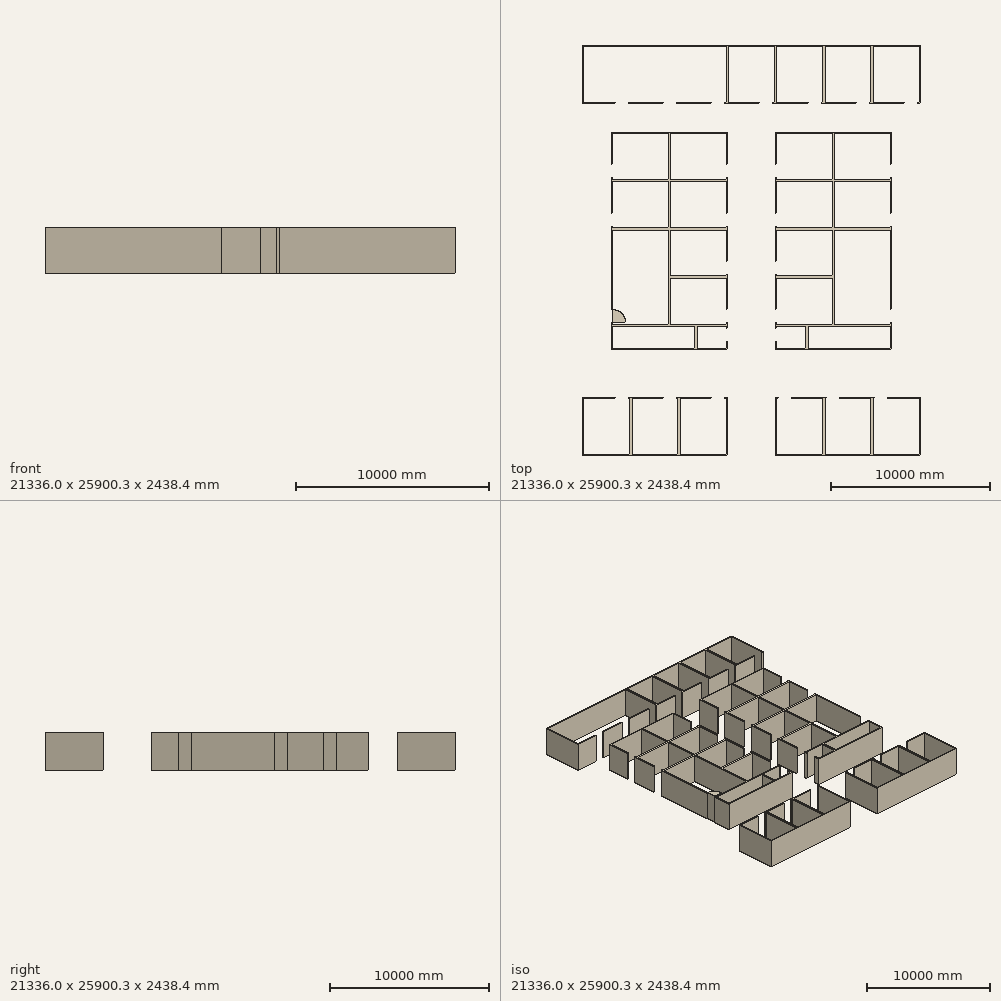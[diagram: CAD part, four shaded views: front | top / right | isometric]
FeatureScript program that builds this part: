
annotation { "Feature Type Name" : "Feature", "Feature Type Description" : "" }
export const myFeature = defineFeature(function(context is Context, id is Id, definition is map)
    precondition{}
    {
        {
            var Q0;
            Q0=qCreatedBy(makeId("Top.planeOp"),FACE);
            var sketch = newSketch(context, id + "F0", { "sketchPlane" : qUnion([Q0])});
            skLineSegment(sketch, "E0.bottom", {"start": v(7665, -2192.75) * mm, "end": v(10713, -2192.75) * mm});
            skLineSegment(sketch, "E0.top", {"start": v(7665, 1464.85) * mm, "end": v(10713, 1464.85) * mm});
            skLineSegment(sketch, "E0.left", {"start": v(7665, -2192.75) * mm, "end": v(7665, 1464.85) * mm});
            skLineSegment(sketch, "E0.right", {"start": v(10713, -2192.75) * mm, "end": v(10713, 1464.85) * mm});
            skLineSegment(sketch, "E1.left", {"start": v(10713, 1464.85) * mm, "end": v(10713, -2192.75) * mm});
            skLineSegment(sketch, "E2.bottom", {"start": v(7665, 6029.3) * mm, "end": v(11322.6, 6029.3) * mm});
            skLineSegment(sketch, "E2.top", {"start": v(7665, 9077.3) * mm, "end": v(11322.6, 9077.3) * mm});
            skLineSegment(sketch, "E2.left", {"start": v(7665, 6029.3) * mm, "end": v(7665, 9077.3) * mm});
            skLineSegment(sketch, "E2.right", {"start": v(11322.6, 6029.3) * mm, "end": v(11322.6, 9077.3) * mm});
            skLineSegment(sketch, "E3.bottom", {"start": v(11322.6, 6029.3) * mm, "end": v(14980.2, 6029.3) * mm});
            skLineSegment(sketch, "E4.bottom", {"start": v(7665, 6029.3) * mm, "end": v(9643.15, 6029.3) * mm});
            skLineSegment(sketch, "E4.top", {"start": v(7665, 4505.3) * mm, "end": v(9643.15, 4505.3) * mm});
            skLineSegment(sketch, "E4.left", {"start": v(7665, 6029.3) * mm, "end": v(7665, 4505.3) * mm});
            skLineSegment(sketch, "E4.right", {"start": v(9643.15, 6029.3) * mm, "end": v(9643.15, 4505.3) * mm});
            skLineSegment(sketch, "E5.bottom", {"start": v(9643.15, 4505.3) * mm, "end": v(14980.2, 4505.3) * mm});
            skLineSegment(sketch, "E5.top", {"start": v(9643.15, 6029.3) * mm, "end": v(14980.2, 6029.3) * mm});
            skLineSegment(sketch, "E5.left", {"start": v(9643.15, 4505.3) * mm, "end": v(9643.15, 6029.3) * mm});
            skLineSegment(sketch, "E5.right", {"start": v(14980.2, 4505.3) * mm, "end": v(14980.2, 6029.3) * mm});
            skLineSegment(sketch, "E6.0", {"start": v(7741.2, -2116.55) * mm, "end": v(10636.8, -2116.55) * mm});
            skLineSegment(sketch, "E6.1", {"start": v(7741.2, -2116.55) * mm, "end": v(7741.2, 1388.65) * mm});
            skLineSegment(sketch, "E6.2", {"start": v(7741.2, 1388.65) * mm, "end": v(10636.8, 1388.65) * mm});
            skLineSegment(sketch, "E6.3", {"start": v(10636.8, 1388.65) * mm, "end": v(10636.8, -2116.55) * mm});
            skLineSegment(sketch, "E7", {"start": v(7842.8, 1388.65) * mm, "end": v(7842.8, 1464.85) * mm});
            skLineSegment(sketch, "E8", {"start": v(8655.6, 1388.65) * mm, "end": v(8655.6, 1464.85) * mm});
            skLineSegment(sketch, "E9", {"start": v(8655.6, 1388.65) * mm, "end": v(8655.6, 575.85) * mm});
            skArc(sketch, "E10", {"start": v(8655.6, 575.85) * mm, "mid": v(8080.86, 813.91) * mm, "end": v(7842.8, 1388.65) * mm});
            skLineSegment(sketch, "E11.0", {"start": v(7741.2, 9001.1) * mm, "end": v(11246.4, 9001.1) * mm});
            skLineSegment(sketch, "E11.1", {"start": v(7741.2, 6105.5) * mm, "end": v(7741.2, 9001.1) * mm});
            skLineSegment(sketch, "E11.2", {"start": v(7741.2, 6105.5) * mm, "end": v(11246.4, 6105.5) * mm});
            skLineSegment(sketch, "E11.3", {"start": v(11246.4, 6105.5) * mm, "end": v(11246.4, 9001.1) * mm});
            skLineSegment(sketch, "E12", {"start": v(7741.2, 6207.1) * mm, "end": v(7665, 6207.1) * mm});
            skLineSegment(sketch, "E13", {"start": v(7741.2, 7019.9) * mm, "end": v(7665, 7019.9) * mm});
            skLineSegment(sketch, "E14", {"start": v(7741.2, 7019.9) * mm, "end": v(8554, 7019.9) * mm});
            skArc(sketch, "E15", {"start": v(8554, 7019.9) * mm, "mid": v(8315.93, 6445.17) * mm, "end": v(7741.2, 6207.1) * mm});
            skArc(sketch, "E16.0.1.0", {"start": v(8554, 10067.9) * mm, "mid": v(8315.93, 9493.17) * mm, "end": v(7741.2, 9255.1) * mm});
            skLineSegment(sketch, "E16.0.1.1", {"start": v(7741.2, 12049.1) * mm, "end": v(11246.4, 12049.1) * mm});
            skLineSegment(sketch, "E16.0.1.2", {"start": v(11322.6, 9077.3) * mm, "end": v(11322.6, 12125.3) * mm});
            skLineSegment(sketch, "E16.0.1.3", {"start": v(7741.2, 10067.9) * mm, "end": v(8554, 10067.9) * mm});
            skLineSegment(sketch, "E16.0.1.6", {"start": v(11246.4, 9153.5) * mm, "end": v(11246.4, 12049.1) * mm});
            skLineSegment(sketch, "E16.0.1.10", {"start": v(7741.2, 9153.5) * mm, "end": v(11246.4, 9153.5) * mm});
            skLineSegment(sketch, "E16.0.1.13", {"start": v(11322.6, 9077.3) * mm, "end": v(11322.6, 12125.3) * mm});
            skLineSegment(sketch, "E16.0.1.14", {"start": v(7741.2, 9255.1) * mm, "end": v(7665, 9255.1) * mm});
            skLineSegment(sketch, "E16.0.1.15", {"start": v(7741.2, 10067.9) * mm, "end": v(7665, 10067.9) * mm});
            skArc(sketch, "E16.0.2.0", {"start": v(8554, 13115.9) * mm, "mid": v(8315.93, 12541.17) * mm, "end": v(7741.2, 12303.1) * mm});
            skLineSegment(sketch, "E16.0.2.1", {"start": v(7741.2, 15097.1) * mm, "end": v(11246.4, 15097.1) * mm});
            skLineSegment(sketch, "E16.0.2.2", {"start": v(11322.6, 12125.3) * mm, "end": v(11322.6, 14975.18) * mm});
            skLineSegment(sketch, "E16.0.2.3", {"start": v(7741.2, 13115.9) * mm, "end": v(8554, 13115.9) * mm});
            skLineSegment(sketch, "E16.0.2.6", {"start": v(11246.4, 12201.5) * mm, "end": v(11246.4, 15097.1) * mm});
            skLineSegment(sketch, "E16.0.2.7", {"start": v(7665, 12125.3) * mm, "end": v(7665, 14975.18) * mm});
            skLineSegment(sketch, "E16.0.2.10", {"start": v(7741.2, 12201.5) * mm, "end": v(11246.4, 12201.5) * mm});
            skLineSegment(sketch, "E16.0.2.11", {"start": v(7741.2, 12201.5) * mm, "end": v(7741.2, 15097.1) * mm});
            skLineSegment(sketch, "E16.0.2.13", {"start": v(11322.6, 12125.3) * mm, "end": v(11322.6, 15173.3) * mm});
            skLineSegment(sketch, "E16.0.2.14", {"start": v(7741.2, 12303.1) * mm, "end": v(7665, 12303.1) * mm});
            skLineSegment(sketch, "E16.0.2.15", {"start": v(7741.2, 13115.9) * mm, "end": v(7665, 13115.9) * mm});
            skArc(sketch, "E16.0.3.0", {"start": v(8554, 16163.9) * mm, "mid": v(8315.93, 15589.17) * mm, "end": v(7741.2, 15351.1) * mm});
            skLineSegment(sketch, "E16.0.3.1", {"start": v(7741.2, 18145.1) * mm, "end": v(11246.4, 18145.1) * mm});
            skLineSegment(sketch, "E16.0.3.2", {"start": v(11322.6, 15173.3) * mm, "end": v(11322.6, 18221.3) * mm});
            skLineSegment(sketch, "E16.0.3.3", {"start": v(7741.2, 16163.9) * mm, "end": v(8554, 16163.9) * mm});
            skLineSegment(sketch, "E16.0.3.4", {"start": v(7665, 15173.3) * mm, "end": v(11322.6, 15173.3) * mm});
            skLineSegment(sketch, "E16.0.3.6", {"start": v(11246.4, 15249.5) * mm, "end": v(11246.4, 18145.1) * mm});
            skLineSegment(sketch, "E16.0.3.7", {"start": v(7665, 15173.3) * mm, "end": v(7665, 18221.3) * mm});
            skLineSegment(sketch, "E16.0.3.8", {"start": v(7665, 18221.3) * mm, "end": v(11322.6, 18221.3) * mm});
            skLineSegment(sketch, "E16.0.3.10", {"start": v(7741.2, 15249.5) * mm, "end": v(11246.4, 15249.5) * mm});
            skLineSegment(sketch, "E16.0.3.11", {"start": v(7741.2, 15249.5) * mm, "end": v(7741.2, 18145.1) * mm});
            skLineSegment(sketch, "E16.0.3.12", {"start": v(7665, 18221.3) * mm, "end": v(11322.6, 18221.3) * mm});
            skLineSegment(sketch, "E16.0.3.13", {"start": v(11322.6, 15173.3) * mm, "end": v(11322.6, 18221.3) * mm});
            skLineSegment(sketch, "E16.0.3.14", {"start": v(7741.2, 15351.1) * mm, "end": v(7665, 15351.1) * mm});
            skLineSegment(sketch, "E16.0.3.15", {"start": v(7741.2, 16163.9) * mm, "end": v(7665, 16163.9) * mm});
            skLineSegment(sketch, "E16.direction1", {"start": v(7665, 6029.3) * mm, "end": v(7665, 6029.3) * mm});
            skLineSegment(sketch, "E16.direction2", {"start": v(7665, 6029.3) * mm, "end": v(7665, 9077.3) * mm, "construction": true});
            skLineSegment(sketch, "E17.left", {"start": v(11322.6, 6029.3) * mm, "end": v(11322.6, 12125.3) * mm});
            skLineSegment(sketch, "E18.MirrorCS", {"start": v(14904, 15351.1) * mm, "end": v(14980.2, 15351.1) * mm});
            skLineSegment(sketch, "E19.MirrorCS", {"start": v(14904, 12303.1) * mm, "end": v(14980.2, 12303.1) * mm});
            skLineSegment(sketch, "E20.MirrorCS", {"start": v(14904, 13115.9) * mm, "end": v(14980.2, 13115.9) * mm});
            skLineSegment(sketch, "E21.MirrorCS", {"start": v(14904, 16163.9) * mm, "end": v(14980.2, 16163.9) * mm});
            skLineSegment(sketch, "E22.MirrorCS", {"start": v(14980.2, 15173.3) * mm, "end": v(11322.6, 15173.3) * mm});
            skLineSegment(sketch, "E23.MirrorCS", {"start": v(14980.2, 18221.3) * mm, "end": v(11322.6, 18221.3) * mm});
            skLineSegment(sketch, "E24.MirrorCS", {"start": v(14904, 15097.1) * mm, "end": v(11398.8, 15097.1) * mm});
            skLineSegment(sketch, "E25.MirrorCS", {"start": v(14904, 18145.1) * mm, "end": v(11398.8, 18145.1) * mm});
            skArc(sketch, "E26.MirrorCS", {"start": v(14091.2, 13115.9) * mm, "mid": v(14329.26, 12541.17) * mm, "end": v(14904, 12303.1) * mm});
            skArc(sketch, "E27.MirrorCS", {"start": v(14091.2, 16163.9) * mm, "mid": v(14329.26, 15589.17) * mm, "end": v(14904, 15351.1) * mm});
            skLineSegment(sketch, "E28.MirrorCS", {"start": v(14980.2, 15173.3) * mm, "end": v(14980.2, 18221.3) * mm});
            skLineSegment(sketch, "E29.MirrorCS", {"start": v(14904, 13115.9) * mm, "end": v(14091.2, 13115.9) * mm});
            skLineSegment(sketch, "E30.MirrorCS", {"start": v(14904, 16163.9) * mm, "end": v(14091.2, 16163.9) * mm});
            skLineSegment(sketch, "E31.MirrorCS", {"start": v(14980.2, 12125.3) * mm, "end": v(14980.2, 14975.18) * mm});
            skLineSegment(sketch, "E32.MirrorCS", {"start": v(14980.2, 6029.3) * mm, "end": v(13002.04, 6029.3) * mm});
            skLineSegment(sketch, "E33.MirrorCS", {"start": v(11398.8, 12201.5) * mm, "end": v(11398.8, 15097.1) * mm});
            skLineSegment(sketch, "E34.MirrorCS", {"start": v(11398.8, 15249.5) * mm, "end": v(11398.8, 18145.1) * mm});
            skLineSegment(sketch, "E35.MirrorCS", {"start": v(14980.2, 6029.3) * mm, "end": v(11322.6, 6029.3) * mm});
            skLineSegment(sketch, "E36.MirrorCS", {"start": v(14904, 15249.5) * mm, "end": v(14904, 18145.1) * mm});
            skLineSegment(sketch, "E37.MirrorCS", {"start": v(14904, 12201.5) * mm, "end": v(14904, 15097.1) * mm});
            skLineSegment(sketch, "E38.MirrorCS", {"start": v(14904, 15249.5) * mm, "end": v(11398.8, 15249.5) * mm});
            skLineSegment(sketch, "E39.MirrorCS", {"start": v(14904, 12201.5) * mm, "end": v(11398.8, 12201.5) * mm});
            skLineSegment(sketch, "E40.MirrorCS", {"start": v(14980.2, 4505.3) * mm, "end": v(13002.04, 4505.3) * mm});
            skLineSegment(sketch, "E41.0", {"start": v(7741.2, 4581.5) * mm, "end": v(9566.95, 4581.5) * mm});
            skLineSegment(sketch, "E41.1", {"start": v(7741.2, 5953.1) * mm, "end": v(7741.2, 4581.5) * mm});
            skLineSegment(sketch, "E41.2", {"start": v(7741.2, 5953.1) * mm, "end": v(9566.95, 5953.1) * mm});
            skLineSegment(sketch, "E41.3", {"start": v(9566.95, 5953.1) * mm, "end": v(9566.95, 4581.5) * mm});
            skLineSegment(sketch, "E42.0", {"start": v(9719.35, 4581.5) * mm, "end": v(14904, 4581.5) * mm});
            skLineSegment(sketch, "E42.1", {"start": v(9719.35, 5953.1) * mm, "end": v(9719.35, 4581.5) * mm});
            skLineSegment(sketch, "E42.2", {"start": v(9719.35, 5953.1) * mm, "end": v(14904, 5953.1) * mm});
            skLineSegment(sketch, "E42.3", {"start": v(14904, 4581.5) * mm, "end": v(14904, 5953.1) * mm});
            skLineSegment(sketch, "E43", {"start": v(7741.2, 5851.5) * mm, "end": v(7665, 5851.5) * mm});
            skLineSegment(sketch, "E44", {"start": v(7741.2, 5038.7) * mm, "end": v(7665, 5038.7) * mm});
            skLineSegment(sketch, "E45", {"start": v(7741.2, 5851.5) * mm, "end": v(8554, 5851.5) * mm});
            skArc(sketch, "E46", {"start": v(8554, 5851.5) * mm, "mid": v(8315.93, 5276.77) * mm, "end": v(7741.2, 5038.7) * mm});
            skLineSegment(sketch, "E47.1.0.0", {"start": v(10789.2, -2116.55) * mm, "end": v(10789.2, 1388.65) * mm});
            skLineSegment(sketch, "E47.1.0.1", {"start": v(10789.2, 1388.65) * mm, "end": v(13684.8, 1388.65) * mm});
            skLineSegment(sketch, "E47.1.0.2", {"start": v(10789.2, -2116.55) * mm, "end": v(13684.8, -2116.55) * mm});
            skLineSegment(sketch, "E47.1.0.3", {"start": v(13684.8, 1388.65) * mm, "end": v(13684.8, -2116.55) * mm});
            skLineSegment(sketch, "E47.1.0.4", {"start": v(11703.6, 1388.65) * mm, "end": v(11703.6, 575.85) * mm});
            skLineSegment(sketch, "E47.1.0.5", {"start": v(10713, -2192.75) * mm, "end": v(13761, -2192.75) * mm});
            skLineSegment(sketch, "E47.1.0.6", {"start": v(10713, 1464.85) * mm, "end": v(13761, 1464.85) * mm});
            skArc(sketch, "E47.1.0.8", {"start": v(11703.6, 575.85) * mm, "mid": v(11128.86, 813.91) * mm, "end": v(10890.8, 1388.65) * mm});
            skLineSegment(sketch, "E47.1.0.9", {"start": v(13761, 1464.85) * mm, "end": v(13761, -2192.75) * mm});
            skLineSegment(sketch, "E47.1.0.10", {"start": v(10890.8, 1388.65) * mm, "end": v(10890.8, 1464.85) * mm});
            skLineSegment(sketch, "E47.1.0.11", {"start": v(11703.6, 1388.65) * mm, "end": v(11703.6, 1464.85) * mm});
            skLineSegment(sketch, "E47.1.0.12", {"start": v(13761, -2192.75) * mm, "end": v(13761, 1464.85) * mm});
            skLineSegment(sketch, "E47.2.0.0", {"start": v(13837.2, -2116.55) * mm, "end": v(13837.2, 1388.65) * mm});
            skLineSegment(sketch, "E47.2.0.1", {"start": v(13837.2, 1388.65) * mm, "end": v(16732.8, 1388.65) * mm});
            skLineSegment(sketch, "E47.2.0.2", {"start": v(13837.2, -2116.55) * mm, "end": v(16732.8, -2116.55) * mm});
            skLineSegment(sketch, "E47.2.0.3", {"start": v(16732.8, 1388.65) * mm, "end": v(16732.8, -2116.55) * mm});
            skLineSegment(sketch, "E47.2.0.4", {"start": v(14751.6, 1388.65) * mm, "end": v(14751.6, 575.85) * mm});
            skLineSegment(sketch, "E47.2.0.5", {"start": v(13761, -2192.75) * mm, "end": v(16809, -2192.75) * mm});
            skLineSegment(sketch, "E47.2.0.6", {"start": v(13761, 1464.85) * mm, "end": v(16809, 1464.85) * mm});
            skLineSegment(sketch, "E47.2.0.7", {"start": v(13761, -2192.75) * mm, "end": v(13761, 1464.85) * mm});
            skArc(sketch, "E47.2.0.8", {"start": v(14751.6, 575.85) * mm, "mid": v(14176.86, 813.91) * mm, "end": v(13938.8, 1388.65) * mm});
            skLineSegment(sketch, "E47.2.0.9", {"start": v(16809, 1464.85) * mm, "end": v(16809, -2192.75) * mm});
            skLineSegment(sketch, "E47.2.0.10", {"start": v(13938.8, 1388.65) * mm, "end": v(13938.8, 1464.85) * mm});
            skLineSegment(sketch, "E47.2.0.11", {"start": v(14751.6, 1388.65) * mm, "end": v(14751.6, 1464.85) * mm});
            skLineSegment(sketch, "E47.2.0.12", {"start": v(16809, -2192.75) * mm, "end": v(16809, 1464.85) * mm});
            skLineSegment(sketch, "E47.direction1", {"start": v(7665, -2192.75) * mm, "end": v(10713, -2192.75) * mm, "construction": true});
            skLineSegment(sketch, "E48.1.0.9", {"start": v(7665.05, 20128.44) * mm, "end": v(7665.05, 23786.04) * mm});
            skLineSegment(sketch, "E48.1.0.12", {"start": v(7665.05, 23707.55) * mm, "end": v(7665.05, 20049.95) * mm});
            skLineSegment(sketch, "E48.2.0.0", {"start": v(7588.85, 23631.35) * mm, "end": v(7588.85, 20126.15) * mm});
            skLineSegment(sketch, "E48.2.0.1", {"start": v(7588.85, 20126.15) * mm, "end": v(4693.25, 20126.15) * mm});
            skLineSegment(sketch, "E48.2.0.2", {"start": v(7588.85, 23631.35) * mm, "end": v(4693.25, 23631.35) * mm});
            skLineSegment(sketch, "E48.2.0.3", {"start": v(4693.25, 20126.15) * mm, "end": v(4693.25, 23631.35) * mm});
            skLineSegment(sketch, "E48.2.0.4", {"start": v(6674.45, 20126.15) * mm, "end": v(6674.45, 20938.95) * mm});
            skLineSegment(sketch, "E48.2.0.5", {"start": v(7665.05, 23707.55) * mm, "end": v(4617.05, 23707.55) * mm});
            skLineSegment(sketch, "E48.2.0.6", {"start": v(7665.05, 20049.95) * mm, "end": v(4617.05, 20049.95) * mm});
            skLineSegment(sketch, "E48.2.0.7", {"start": v(7665.05, 23707.55) * mm, "end": v(7665.05, 20049.95) * mm});
            skArc(sketch, "E48.2.0.8", {"start": v(6674.45, 20938.95) * mm, "mid": v(7249.19, 20700.89) * mm, "end": v(7487.25, 20126.15) * mm});
            skLineSegment(sketch, "E48.2.0.9", {"start": v(4617.05, 20049.95) * mm, "end": v(4617.05, 23707.55) * mm});
            skLineSegment(sketch, "E48.2.0.10", {"start": v(7487.25, 20126.15) * mm, "end": v(7487.25, 20049.95) * mm});
            skLineSegment(sketch, "E48.2.0.11", {"start": v(6674.45, 20126.15) * mm, "end": v(6674.45, 20049.95) * mm});
            skLineSegment(sketch, "E48.2.0.12", {"start": v(4617.05, 23707.55) * mm, "end": v(4617.05, 20049.95) * mm});
            skLineSegment(sketch, "E49.1.0.1", {"start": v(10636.85, 23631.35) * mm, "end": v(10636.85, 20126.15) * mm});
            skLineSegment(sketch, "E49.1.0.2", {"start": v(10636.85, 20126.15) * mm, "end": v(7741.25, 20126.15) * mm});
            skLineSegment(sketch, "E49.1.0.3", {"start": v(7741.25, 20126.15) * mm, "end": v(7741.25, 23631.35) * mm});
            skLineSegment(sketch, "E49.1.0.4", {"start": v(10636.85, 23631.35) * mm, "end": v(7741.25, 23631.35) * mm});
            skLineSegment(sketch, "E49.1.0.5", {"start": v(9722.45, 20126.15) * mm, "end": v(9722.45, 20938.95) * mm});
            skLineSegment(sketch, "E49.1.0.6", {"start": v(10713.05, 23707.55) * mm, "end": v(7665.05, 23707.55) * mm});
            skLineSegment(sketch, "E49.1.0.7", {"start": v(10713.05, 20049.95) * mm, "end": v(7665.05, 20049.95) * mm});
            skLineSegment(sketch, "E49.1.0.8", {"start": v(10713.05, 23707.55) * mm, "end": v(10713.05, 20049.95) * mm});
            skArc(sketch, "E49.1.0.9", {"start": v(9722.45, 20938.95) * mm, "mid": v(10297.19, 20700.89) * mm, "end": v(10535.25, 20126.15) * mm});
            skLineSegment(sketch, "E49.1.0.10", {"start": v(7665.05, 20049.95) * mm, "end": v(7665.05, 23707.55) * mm});
            skLineSegment(sketch, "E49.1.0.11", {"start": v(10713.05, 23707.55) * mm, "end": v(10713.05, 20049.95) * mm});
            skLineSegment(sketch, "E49.1.0.12", {"start": v(10535.25, 20126.15) * mm, "end": v(10535.25, 20049.95) * mm});
            skLineSegment(sketch, "E49.1.0.13", {"start": v(10713.05, 20128.44) * mm, "end": v(10713.05, 23786.04) * mm});
            skLineSegment(sketch, "E49.1.0.14", {"start": v(9722.45, 20126.15) * mm, "end": v(9722.45, 20049.95) * mm});
            skLineSegment(sketch, "E49.2.0.0", {"start": v(10713.05, 23707.55) * mm, "end": v(10713.05, 20049.95) * mm});
            skLineSegment(sketch, "E49.2.0.1", {"start": v(13684.85, 23631.35) * mm, "end": v(13684.85, 20126.15) * mm});
            skLineSegment(sketch, "E49.2.0.2", {"start": v(13684.85, 20126.15) * mm, "end": v(10789.25, 20126.15) * mm});
            skLineSegment(sketch, "E49.2.0.3", {"start": v(10789.25, 20126.15) * mm, "end": v(10789.25, 23631.35) * mm});
            skLineSegment(sketch, "E49.2.0.4", {"start": v(13684.85, 23631.35) * mm, "end": v(10789.25, 23631.35) * mm});
            skLineSegment(sketch, "E49.2.0.5", {"start": v(12770.45, 20126.15) * mm, "end": v(12770.45, 20938.95) * mm});
            skLineSegment(sketch, "E49.2.0.6", {"start": v(13761.05, 23707.55) * mm, "end": v(10713.05, 23707.55) * mm});
            skLineSegment(sketch, "E49.2.0.7", {"start": v(13761.05, 20049.95) * mm, "end": v(10713.05, 20049.95) * mm});
            skLineSegment(sketch, "E49.2.0.8", {"start": v(13761.05, 23707.55) * mm, "end": v(13761.05, 20049.95) * mm});
            skArc(sketch, "E49.2.0.9", {"start": v(12770.45, 20938.95) * mm, "mid": v(13345.19, 20700.89) * mm, "end": v(13583.25, 20126.15) * mm});
            skLineSegment(sketch, "E49.2.0.10", {"start": v(10713.05, 20049.95) * mm, "end": v(10713.05, 23707.55) * mm});
            skLineSegment(sketch, "E49.2.0.11", {"start": v(13761.05, 23707.55) * mm, "end": v(13761.05, 20049.95) * mm});
            skLineSegment(sketch, "E49.2.0.12", {"start": v(13583.25, 20126.15) * mm, "end": v(13583.25, 20049.95) * mm});
            skLineSegment(sketch, "E49.2.0.13", {"start": v(13761.05, 20128.44) * mm, "end": v(13761.05, 23786.04) * mm});
            skLineSegment(sketch, "E49.2.0.14", {"start": v(12770.45, 20126.15) * mm, "end": v(12770.45, 20049.95) * mm});
            skLineSegment(sketch, "E49.3.0.0", {"start": v(13761.05, 23707.55) * mm, "end": v(13761.05, 20049.95) * mm});
            skLineSegment(sketch, "E49.3.0.1", {"start": v(16732.85, 23631.35) * mm, "end": v(16732.85, 20126.15) * mm});
            skLineSegment(sketch, "E49.3.0.2", {"start": v(16732.85, 20126.15) * mm, "end": v(13837.25, 20126.15) * mm});
            skLineSegment(sketch, "E49.3.0.3", {"start": v(13837.25, 20126.15) * mm, "end": v(13837.25, 23631.35) * mm});
            skLineSegment(sketch, "E49.3.0.4", {"start": v(16732.85, 23631.35) * mm, "end": v(13837.25, 23631.35) * mm});
            skLineSegment(sketch, "E49.3.0.5", {"start": v(15818.45, 20126.15) * mm, "end": v(15818.45, 20938.95) * mm});
            skLineSegment(sketch, "E49.3.0.6", {"start": v(16809.05, 23707.55) * mm, "end": v(13761.05, 23707.55) * mm});
            skLineSegment(sketch, "E49.3.0.7", {"start": v(16809.05, 20049.95) * mm, "end": v(13761.05, 20049.95) * mm});
            skLineSegment(sketch, "E49.3.0.8", {"start": v(16809.05, 23707.55) * mm, "end": v(16809.05, 20049.95) * mm});
            skArc(sketch, "E49.3.0.9", {"start": v(15818.45, 20938.95) * mm, "mid": v(16393.19, 20700.89) * mm, "end": v(16631.25, 20126.15) * mm});
            skLineSegment(sketch, "E49.3.0.10", {"start": v(13761.05, 20049.95) * mm, "end": v(13761.05, 23707.55) * mm});
            skLineSegment(sketch, "E49.3.0.11", {"start": v(16809.05, 23707.55) * mm, "end": v(16809.05, 20049.95) * mm});
            skLineSegment(sketch, "E49.3.0.12", {"start": v(16631.25, 20126.15) * mm, "end": v(16631.25, 20049.95) * mm});
            skLineSegment(sketch, "E49.3.0.13", {"start": v(16809.05, 20128.44) * mm, "end": v(16809.05, 23786.04) * mm});
            skLineSegment(sketch, "E49.3.0.14", {"start": v(15818.45, 20126.15) * mm, "end": v(15818.45, 20049.95) * mm});
            skLineSegment(sketch, "E49.direction1", {"start": v(4617.05, 20049.95) * mm, "end": v(7665.05, 20049.95) * mm, "construction": true});
            skLineSegment(sketch, "E50.1.0.0", {"start": v(1569.05, 20049.95) * mm, "end": v(4617.05, 20049.95) * mm, "construction": true});
            skArc(sketch, "E50.1.0.1", {"start": v(3626.45, 20938.95) * mm, "mid": v(4201.19, 20700.89) * mm, "end": v(4439.25, 20126.15) * mm});
            skLineSegment(sketch, "E50.1.0.2", {"start": v(4617.05, 23707.55) * mm, "end": v(1569.05, 23707.55) * mm});
            skLineSegment(sketch, "E50.1.0.3", {"start": v(4540.85, 23631.35) * mm, "end": v(4540.85, 20126.15) * mm});
            skLineSegment(sketch, "E50.1.0.4", {"start": v(3626.45, 20126.15) * mm, "end": v(3626.45, 20938.95) * mm});
            skLineSegment(sketch, "E50.1.0.8", {"start": v(4540.85, 20126.15) * mm, "end": v(1645.25, 20126.15) * mm});
            skLineSegment(sketch, "E50.1.0.9", {"start": v(4540.85, 23631.35) * mm, "end": v(1645.25, 23631.35) * mm});
            skLineSegment(sketch, "E50.1.0.11", {"start": v(4617.05, 20049.95) * mm, "end": v(1569.05, 20049.95) * mm});
            skLineSegment(sketch, "E50.1.0.12", {"start": v(4617.05, 20128.44) * mm, "end": v(4617.05, 23786.04) * mm});
            skLineSegment(sketch, "E50.1.0.13", {"start": v(4439.25, 20126.15) * mm, "end": v(4439.25, 20049.95) * mm});
            skLineSegment(sketch, "E50.1.0.15", {"start": v(3626.45, 20126.15) * mm, "end": v(3626.45, 20049.95) * mm});
            skLineSegment(sketch, "E50.2.0.0", {"start": v(-1478.95, 20049.95) * mm, "end": v(1569.05, 20049.95) * mm, "construction": true});
            skArc(sketch, "E50.2.0.1", {"start": v(578.45, 20938.95) * mm, "mid": v(1153.19, 20700.89) * mm, "end": v(1391.25, 20126.15) * mm});
            skLineSegment(sketch, "E50.2.0.2", {"start": v(1569.05, 23707.55) * mm, "end": v(-1478.95, 23707.55) * mm});
            skLineSegment(sketch, "E50.2.0.4", {"start": v(578.45, 20126.15) * mm, "end": v(578.45, 20938.95) * mm});
            skLineSegment(sketch, "E50.2.0.8", {"start": v(1492.85, 20126.15) * mm, "end": v(-1402.75, 20126.15) * mm});
            skLineSegment(sketch, "E50.2.0.9", {"start": v(1492.85, 23631.35) * mm, "end": v(-1402.75, 23631.35) * mm});
            skLineSegment(sketch, "E50.2.0.11", {"start": v(1569.05, 20049.95) * mm, "end": v(-1478.95, 20049.95) * mm});
            skLineSegment(sketch, "E50.2.0.13", {"start": v(1391.25, 20126.15) * mm, "end": v(1391.25, 20049.95) * mm});
            skLineSegment(sketch, "E50.2.0.15", {"start": v(578.45, 20126.15) * mm, "end": v(578.45, 20049.95) * mm});
            skLineSegment(sketch, "E50.3.0.0", {"start": v(-4526.95, 20049.95) * mm, "end": v(-1478.95, 20049.95) * mm, "construction": true});
            skArc(sketch, "E50.3.0.1", {"start": v(-2469.55, 20938.95) * mm, "mid": v(-1894.81, 20700.89) * mm, "end": v(-1656.75, 20126.15) * mm});
            skLineSegment(sketch, "E50.3.0.2", {"start": v(-1478.95, 23707.55) * mm, "end": v(-4526.95, 23707.55) * mm});
            skLineSegment(sketch, "E50.3.0.4", {"start": v(-2469.55, 20126.15) * mm, "end": v(-2469.55, 20938.95) * mm});
            skLineSegment(sketch, "E50.3.0.5", {"start": v(-4450.75, 20126.15) * mm, "end": v(-4450.75, 23631.35) * mm});
            skLineSegment(sketch, "E50.3.0.7", {"start": v(-4526.95, 23707.55) * mm, "end": v(-4526.95, 20049.95) * mm});
            skLineSegment(sketch, "E50.3.0.8", {"start": v(-1555.15, 20126.15) * mm, "end": v(-4450.75, 20126.15) * mm});
            skLineSegment(sketch, "E50.3.0.9", {"start": v(-1555.15, 23631.35) * mm, "end": v(-4450.75, 23631.35) * mm});
            skLineSegment(sketch, "E50.3.0.10", {"start": v(-4526.95, 20049.95) * mm, "end": v(-4526.95, 23707.55) * mm});
            skLineSegment(sketch, "E50.3.0.11", {"start": v(-1478.95, 20049.95) * mm, "end": v(-4526.95, 20049.95) * mm});
            skLineSegment(sketch, "E50.3.0.13", {"start": v(-1656.75, 20126.15) * mm, "end": v(-1656.75, 20049.95) * mm});
            skLineSegment(sketch, "E50.3.0.15", {"start": v(-2469.55, 20126.15) * mm, "end": v(-2469.55, 20049.95) * mm});
            skLineSegment(sketch, "E50.direction1", {"start": v(4617.05, 20049.95) * mm, "end": v(1569.05, 20049.95) * mm, "construction": true});
            skLineSegment(sketch, "E51.left", {"start": v(14980.2, 12125.3) * mm, "end": v(14980.2, 6029.3) * mm});
            skLineSegment(sketch, "E51.right", {"start": v(11322.6, 12125.3) * mm, "end": v(11322.6, 6029.3) * mm});
            skLineSegment(sketch, "E52.0", {"start": v(11398.8, 9077.3) * mm, "end": v(11398.8, 12049.1) * mm});
            skLineSegment(sketch, "E52.1", {"start": v(14904, 12049.1) * mm, "end": v(11398.8, 12049.1) * mm});
            skLineSegment(sketch, "E52.2", {"start": v(11398.8, 6105.5) * mm, "end": v(11398.8, 9077.3) * mm});
            skLineSegment(sketch, "E52.3", {"start": v(14904, 6105.5) * mm, "end": v(11398.8, 6105.5) * mm});
            skLineSegment(sketch, "E52.4", {"start": v(14904, 12049.1) * mm, "end": v(14904, 6105.5) * mm});
            skLineSegment(sketch, "E53", {"start": v(14904, 6207.1) * mm, "end": v(14980.2, 6207.1) * mm});
            skLineSegment(sketch, "E54", {"start": v(14904, 6207.1) * mm, "end": v(14091.2, 6207.1) * mm});
            skLineSegment(sketch, "E55", {"start": v(14904, 7019.9) * mm, "end": v(14980.2, 7019.9) * mm});
            skArc(sketch, "E56", {"start": v(14091.2, 6207.1) * mm, "mid": v(14329.26, 6781.84) * mm, "end": v(14904, 7019.9) * mm});
            skLineSegment(sketch, "E57", {"start": v(7665, 15173.3) * mm, "end": v(7665, 14975.18) * mm});
            skLineSegment(sketch, "E58", {"start": v(14980.2, 15173.3) * mm, "end": v(14980.2, 14975.18) * mm});
            skLineSegment(sketch, "E59.MirrorCS", {"start": v(-2622, 6207.1) * mm, "end": v(-2698.2, 6207.1) * mm});
            skLineSegment(sketch, "E60.MirrorCS", {"start": v(959.4, 6029.3) * mm, "end": v(959.4, 12125.3) * mm});
            skLineSegment(sketch, "E61.MirrorCS", {"start": v(4540.8, 6207.1) * mm, "end": v(4617, 6207.1) * mm});
            skLineSegment(sketch, "E62.MirrorCS", {"start": v(4540.8, 9255.1) * mm, "end": v(4617, 9255.1) * mm});
            skLineSegment(sketch, "E63.MirrorCS", {"start": v(-2622, 12303.1) * mm, "end": v(-2698.2, 12303.1) * mm});
            skLineSegment(sketch, "E64.MirrorCS", {"start": v(4540.8, 5851.5) * mm, "end": v(4617, 5851.5) * mm});
            skLineSegment(sketch, "E65.MirrorCS", {"start": v(4540.8, 12303.1) * mm, "end": v(4617, 12303.1) * mm});
            skLineSegment(sketch, "E66.MirrorCS", {"start": v(1035.6, 6105.5) * mm, "end": v(1035.6, 9001.1) * mm});
            skLineSegment(sketch, "E67.MirrorCS", {"start": v(959.4, 9077.3) * mm, "end": v(959.4, 12125.3) * mm});
            skLineSegment(sketch, "E68.MirrorCS", {"start": v(1391.2, 1388.65) * mm, "end": v(1391.2, 1464.85) * mm});
            skLineSegment(sketch, "E69.MirrorCS", {"start": v(-1656.8, 1388.65) * mm, "end": v(-1656.8, 1464.85) * mm});
            skLineSegment(sketch, "E70.MirrorCS", {"start": v(959.4, 12125.3) * mm, "end": v(959.4, 6029.3) * mm});
            skLineSegment(sketch, "E71.MirrorCS", {"start": v(4439.2, 1388.65) * mm, "end": v(4439.2, 1464.85) * mm});
            skLineSegment(sketch, "E72.MirrorCS", {"start": v(959.4, 6029.3) * mm, "end": v(-2698.2, 6029.3) * mm});
            skLineSegment(sketch, "E73.MirrorCS", {"start": v(959.4, 12125.3) * mm, "end": v(959.4, 14975.18) * mm});
            skLineSegment(sketch, "E74.MirrorCS", {"start": v(959.4, 6029.3) * mm, "end": v(959.4, 9077.3) * mm});
            skLineSegment(sketch, "E75.MirrorCS", {"start": v(-1479, -2192.75) * mm, "end": v(-1479, 1464.85) * mm});
            skLineSegment(sketch, "E76.MirrorCS", {"start": v(-2622, 16163.9) * mm, "end": v(-2698.2, 16163.9) * mm});
            skLineSegment(sketch, "E77.MirrorCS", {"start": v(4540.8, 7019.9) * mm, "end": v(4617, 7019.9) * mm});
            skLineSegment(sketch, "E78.MirrorCS", {"start": v(4540.8, 10067.9) * mm, "end": v(4617, 10067.9) * mm});
            skLineSegment(sketch, "E79.MirrorCS", {"start": v(-2622, 13115.9) * mm, "end": v(-2698.2, 13115.9) * mm});
            skLineSegment(sketch, "E80.MirrorCS", {"start": v(959.4, 15173.3) * mm, "end": v(959.4, 18221.3) * mm});
            skLineSegment(sketch, "E81.MirrorCS", {"start": v(-2698.2, 15173.3) * mm, "end": v(-2698.2, 14975.18) * mm});
            skLineSegment(sketch, "E82.MirrorCS", {"start": v(4540.8, 16163.9) * mm, "end": v(4617, 16163.9) * mm});
            skLineSegment(sketch, "E83.MirrorCS", {"start": v(-2622, 15351.1) * mm, "end": v(-2698.2, 15351.1) * mm});
            skLineSegment(sketch, "E84.MirrorCS", {"start": v(4617, 9077.3) * mm, "end": v(959.4, 9077.3) * mm});
            skLineSegment(sketch, "E85.MirrorCS", {"start": v(4540.8, 15351.1) * mm, "end": v(4617, 15351.1) * mm});
            skLineSegment(sketch, "E86.MirrorCS", {"start": v(4540.8, 13115.9) * mm, "end": v(4617, 13115.9) * mm});
            skLineSegment(sketch, "E87.MirrorCS", {"start": v(3626.4, 1388.65) * mm, "end": v(3626.4, 1464.85) * mm});
            skLineSegment(sketch, "E88.MirrorCS", {"start": v(1035.6, 12201.5) * mm, "end": v(1035.6, 15097.1) * mm});
            skLineSegment(sketch, "E89.MirrorCS", {"start": v(4617, 15173.3) * mm, "end": v(4617, 14975.18) * mm});
            skLineSegment(sketch, "E90.MirrorCS", {"start": v(-2698.2, 6029.3) * mm, "end": v(959.4, 6029.3) * mm});
            skLineSegment(sketch, "E91.MirrorCS", {"start": v(-2469.6, 1388.65) * mm, "end": v(-2469.6, 1464.85) * mm});
            skLineSegment(sketch, "E92.MirrorCS", {"start": v(578.4, 1388.65) * mm, "end": v(578.4, 1464.85) * mm});
            skLineSegment(sketch, "E93.MirrorCS", {"start": v(1569, -2192.75) * mm, "end": v(1569, 1464.85) * mm});
            skLineSegment(sketch, "E94.MirrorCS", {"start": v(1035.6, 15249.5) * mm, "end": v(1035.6, 18145.1) * mm});
            skLineSegment(sketch, "E95.MirrorCS", {"start": v(2638.84, 6029.3) * mm, "end": v(-2698.2, 6029.3) * mm});
            skLineSegment(sketch, "E96.MirrorCS", {"start": v(4540.8, 9153.5) * mm, "end": v(1035.6, 9153.5) * mm});
            skLineSegment(sketch, "E97.MirrorCS", {"start": v(4540.8, 5038.7) * mm, "end": v(4617, 5038.7) * mm});
            skLineSegment(sketch, "E98.MirrorCS", {"start": v(-2622, 7019.9) * mm, "end": v(-2698.2, 7019.9) * mm});
            skLineSegment(sketch, "E99.MirrorCS", {"start": v(959.4, 12125.3) * mm, "end": v(959.4, 15173.3) * mm});
            skLineSegment(sketch, "E100.MirrorCS", {"start": v(-1479, 1464.85) * mm, "end": v(-1479, -2192.75) * mm});
            skLineSegment(sketch, "E101.MirrorCS", {"start": v(1645.2, 1388.65) * mm, "end": v(1645.2, -2116.55) * mm});
            skLineSegment(sketch, "E102.MirrorCS", {"start": v(-2698.2, 18221.3) * mm, "end": v(959.4, 18221.3) * mm});
            skLineSegment(sketch, "E103.MirrorCS", {"start": v(4617, -2192.75) * mm, "end": v(1569, -2192.75) * mm});
            skLineSegment(sketch, "E104.MirrorCS", {"start": v(4617, 15173.3) * mm, "end": v(959.4, 15173.3) * mm});
            skLineSegment(sketch, "E105.MirrorCS", {"start": v(2638.84, 4505.3) * mm, "end": v(2638.84, 6029.3) * mm});
            skLineSegment(sketch, "E106.MirrorCS", {"start": v(-2698.2, 6029.3) * mm, "end": v(-720.05, 6029.3) * mm});
            skLineSegment(sketch, "E107.MirrorCS", {"start": v(2562.64, 5953.1) * mm, "end": v(-2622, 5953.1) * mm});
            skLineSegment(sketch, "E108.MirrorCS", {"start": v(4540.8, 5953.1) * mm, "end": v(2715.04, 5953.1) * mm});
            skLineSegment(sketch, "E109.MirrorCS", {"start": v(-4527, 1464.85) * mm, "end": v(-4527, -2192.75) * mm});
            skLineSegment(sketch, "E110.MirrorCS", {"start": v(-2622, 15097.1) * mm, "end": v(883.2, 15097.1) * mm});
            skLineSegment(sketch, "E111.MirrorCS", {"start": v(1035.6, 9153.5) * mm, "end": v(1035.6, 12049.1) * mm});
            skLineSegment(sketch, "E112.MirrorCS", {"start": v(4617, 6029.3) * mm, "end": v(4617, 9077.3) * mm});
            skLineSegment(sketch, "E113.MirrorCS", {"start": v(4617, 18221.3) * mm, "end": v(959.4, 18221.3) * mm});
            skLineSegment(sketch, "E114.MirrorCS", {"start": v(4540.8, 5953.1) * mm, "end": v(4540.8, 4581.5) * mm});
            skLineSegment(sketch, "E115.MirrorCS", {"start": v(1569, -2192.75) * mm, "end": v(-1479, -2192.75) * mm});
            skArc(sketch, "E116.MirrorCS", {"start": v(-2469.6, 575.85) * mm, "mid": v(-1894.87, 813.91) * mm, "end": v(-1656.8, 1388.65) * mm});
            skArc(sketch, "E117.MirrorCS", {"start": v(3728, 7019.9) * mm, "mid": v(3966.06, 6445.17) * mm, "end": v(4540.8, 6207.1) * mm});
            skLineSegment(sketch, "E118.MirrorCS", {"start": v(4540.8, 15097.1) * mm, "end": v(1035.6, 15097.1) * mm});
            skLineSegment(sketch, "E119.MirrorCS", {"start": v(4617, -2192.75) * mm, "end": v(4617, 1464.85) * mm});
            skLineSegment(sketch, "E120.MirrorCS", {"start": v(-2698.2, 4505.3) * mm, "end": v(-2698.2, 6029.3) * mm});
            skLineSegment(sketch, "E121.MirrorCS", {"start": v(4540.8, 4581.5) * mm, "end": v(2715.04, 4581.5) * mm});
            skLineSegment(sketch, "E122.MirrorCS", {"start": v(578.4, 1388.65) * mm, "end": v(578.4, 575.85) * mm});
            skLineSegment(sketch, "E123.MirrorCS", {"start": v(4617, 1464.85) * mm, "end": v(1569, 1464.85) * mm});
            skLineSegment(sketch, "E124.MirrorCS", {"start": v(4540.8, 7019.9) * mm, "end": v(3728, 7019.9) * mm});
            skArc(sketch, "E125.MirrorCS", {"start": v(3728, 13115.9) * mm, "mid": v(3966.06, 12541.17) * mm, "end": v(4540.8, 12303.1) * mm});
            skLineSegment(sketch, "E126.MirrorCS", {"start": v(1569, 1464.85) * mm, "end": v(1569, -2192.75) * mm});
            skLineSegment(sketch, "E127.MirrorCS", {"start": v(2638.84, 6029.3) * mm, "end": v(2638.84, 4505.3) * mm});
            skLineSegment(sketch, "E128.MirrorCS", {"start": v(4617, 6029.3) * mm, "end": v(4617, 4505.3) * mm});
            skLineSegment(sketch, "E129.MirrorCS", {"start": v(4617, 4505.3) * mm, "end": v(2638.84, 4505.3) * mm});
            skLineSegment(sketch, "E130.MirrorCS", {"start": v(-2622, 12049.1) * mm, "end": v(883.2, 12049.1) * mm});
            skLineSegment(sketch, "E131.MirrorCS", {"start": v(883.2, 6105.5) * mm, "end": v(883.2, 9077.3) * mm});
            skArc(sketch, "E132.MirrorCS", {"start": v(-1809.2, 16163.9) * mm, "mid": v(-2047.27, 15589.17) * mm, "end": v(-2622, 15351.1) * mm});
            skLineSegment(sketch, "E133.MirrorCS", {"start": v(-2698.2, 4505.3) * mm, "end": v(-720.05, 4505.3) * mm});
            skLineSegment(sketch, "E134.MirrorCS", {"start": v(-1402.8, 1388.65) * mm, "end": v(-1402.8, -2116.55) * mm});
            skLineSegment(sketch, "E135.MirrorCS", {"start": v(-1479, 1464.85) * mm, "end": v(-4527, 1464.85) * mm});
            skLineSegment(sketch, "E136.MirrorCS", {"start": v(4540.8, 16163.9) * mm, "end": v(3728, 16163.9) * mm});
            skLineSegment(sketch, "E137.MirrorCS", {"start": v(-1555.2, 1388.65) * mm, "end": v(-4450.8, 1388.65) * mm});
            skLineSegment(sketch, "E138.MirrorCS", {"start": v(4617, -2192.75) * mm, "end": v(1569, -2192.75) * mm, "construction": true});
            skLineSegment(sketch, "E139.MirrorCS", {"start": v(4617, 6029.3) * mm, "end": v(4617, 9077.3) * mm, "construction": true});
            skLineSegment(sketch, "E140.MirrorCS", {"start": v(-2622, 15249.5) * mm, "end": v(-2622, 18145.1) * mm});
            skLineSegment(sketch, "E141.MirrorCS", {"start": v(883.2, 9077.3) * mm, "end": v(883.2, 12049.1) * mm});
            skLineSegment(sketch, "E142.MirrorCS", {"start": v(4540.8, 5851.5) * mm, "end": v(3728, 5851.5) * mm});
            skLineSegment(sketch, "E143.MirrorCS", {"start": v(2638.84, 4505.3) * mm, "end": v(-2698.2, 4505.3) * mm});
            skLineSegment(sketch, "E144.MirrorCS", {"start": v(4540.8, 9001.1) * mm, "end": v(1035.6, 9001.1) * mm});
            skArc(sketch, "E145.MirrorCS", {"start": v(-1809.2, 13115.9) * mm, "mid": v(-2047.27, 12541.17) * mm, "end": v(-2622, 12303.1) * mm});
            skLineSegment(sketch, "E146.MirrorCS", {"start": v(-2622, 12201.5) * mm, "end": v(883.2, 12201.5) * mm});
            skLineSegment(sketch, "E147.MirrorCS", {"start": v(1492.8, -2116.55) * mm, "end": v(-1402.8, -2116.55) * mm});
            skLineSegment(sketch, "E148.MirrorCS", {"start": v(-1479, -2192.75) * mm, "end": v(-4527, -2192.75) * mm});
            skLineSegment(sketch, "E149.MirrorCS", {"start": v(-2698.2, 12125.3) * mm, "end": v(-2698.2, 6029.3) * mm});
            skLineSegment(sketch, "E150.MirrorCS", {"start": v(-2622, 18145.1) * mm, "end": v(883.2, 18145.1) * mm});
            skLineSegment(sketch, "E151.MirrorCS", {"start": v(-2622, 15249.5) * mm, "end": v(883.2, 15249.5) * mm});
            skLineSegment(sketch, "E152.MirrorCS", {"start": v(-1555.2, -2116.55) * mm, "end": v(-1555.2, 1388.65) * mm});
            skArc(sketch, "E153.MirrorCS", {"start": v(3626.4, 575.85) * mm, "mid": v(4201.13, 813.91) * mm, "end": v(4439.2, 1388.65) * mm});
            skLineSegment(sketch, "E154.MirrorCS", {"start": v(-2469.6, 1388.65) * mm, "end": v(-2469.6, 575.85) * mm});
            skLineSegment(sketch, "E155.MirrorCS", {"start": v(1492.8, 1388.65) * mm, "end": v(-1402.8, 1388.65) * mm});
            skLineSegment(sketch, "E156.MirrorCS", {"start": v(4540.8, 18145.1) * mm, "end": v(1035.6, 18145.1) * mm});
            skLineSegment(sketch, "E157.MirrorCS", {"start": v(4617, 6029.3) * mm, "end": v(959.4, 6029.3) * mm});
            skLineSegment(sketch, "E158.MirrorCS", {"start": v(4617, 12125.3) * mm, "end": v(4617, 14975.18) * mm});
            skLineSegment(sketch, "E159.MirrorCS", {"start": v(-2622, 12201.5) * mm, "end": v(-2622, 15097.1) * mm});
            skLineSegment(sketch, "E160.MirrorCS", {"start": v(883.2, 15249.5) * mm, "end": v(883.2, 18145.1) * mm});
            skLineSegment(sketch, "E161.MirrorCS", {"start": v(3626.4, 1388.65) * mm, "end": v(3626.4, 575.85) * mm});
            skLineSegment(sketch, "E162.MirrorCS", {"start": v(4540.8, 12201.5) * mm, "end": v(4540.8, 15097.1) * mm});
            skLineSegment(sketch, "E163.MirrorCS", {"start": v(-1555.2, -2116.55) * mm, "end": v(-4450.8, -2116.55) * mm});
            skArc(sketch, "E164.MirrorCS", {"start": v(3728, 5851.5) * mm, "mid": v(3966.06, 5276.77) * mm, "end": v(4540.8, 5038.7) * mm});
            skLineSegment(sketch, "E165.MirrorCS", {"start": v(4540.8, 6105.5) * mm, "end": v(4540.8, 9001.1) * mm});
            skArc(sketch, "E166.MirrorCS", {"start": v(-1809.2, 6207.1) * mm, "mid": v(-2047.27, 6781.84) * mm, "end": v(-2622, 7019.9) * mm});
            skArc(sketch, "E167.MirrorCS", {"start": v(3728, 16163.9) * mm, "mid": v(3966.06, 15589.17) * mm, "end": v(4540.8, 15351.1) * mm});
            skLineSegment(sketch, "E168.MirrorCS", {"start": v(-2622, 6105.5) * mm, "end": v(883.2, 6105.5) * mm});
            skLineSegment(sketch, "E169.MirrorCS", {"start": v(-2622, 6207.1) * mm, "end": v(-1809.2, 6207.1) * mm});
            skLineSegment(sketch, "E170.MirrorCS", {"start": v(883.2, 12201.5) * mm, "end": v(883.2, 15097.1) * mm});
            skLineSegment(sketch, "E171.MirrorCS", {"start": v(-2622, 4581.5) * mm, "end": v(-2622, 5953.1) * mm});
            skLineSegment(sketch, "E172.MirrorCS", {"start": v(4540.8, 6105.5) * mm, "end": v(1035.6, 6105.5) * mm});
            skLineSegment(sketch, "E173.MirrorCS", {"start": v(-2698.2, 15173.3) * mm, "end": v(-2698.2, 18221.3) * mm});
            skLineSegment(sketch, "E174.MirrorCS", {"start": v(1569, 1464.85) * mm, "end": v(-1479, 1464.85) * mm});
            skArc(sketch, "E175.MirrorCS", {"start": v(3728, 10067.9) * mm, "mid": v(3966.06, 9493.17) * mm, "end": v(4540.8, 9255.1) * mm});
            skLineSegment(sketch, "E176.MirrorCS", {"start": v(4617, 15173.3) * mm, "end": v(4617, 18221.3) * mm});
            skLineSegment(sketch, "E177.MirrorCS", {"start": v(4540.8, -2116.55) * mm, "end": v(1645.2, -2116.55) * mm});
            skLineSegment(sketch, "E178.MirrorCS", {"start": v(-4527, -2192.75) * mm, "end": v(-4527, 1464.85) * mm});
            skLineSegment(sketch, "E179.MirrorCS", {"start": v(4540.8, 15249.5) * mm, "end": v(4540.8, 18145.1) * mm});
            skLineSegment(sketch, "E180.MirrorCS", {"start": v(4540.8, 12201.5) * mm, "end": v(1035.6, 12201.5) * mm});
            skLineSegment(sketch, "E181.MirrorCS", {"start": v(-2698.2, 12125.3) * mm, "end": v(-2698.2, 14975.18) * mm});
            skLineSegment(sketch, "E182.MirrorCS", {"start": v(2562.64, 5953.1) * mm, "end": v(2562.64, 4581.5) * mm});
            skLineSegment(sketch, "E183.MirrorCS", {"start": v(4540.8, 10067.9) * mm, "end": v(3728, 10067.9) * mm});
            skLineSegment(sketch, "E184.MirrorCS", {"start": v(1492.8, -2116.55) * mm, "end": v(1492.8, 1388.65) * mm});
            skLineSegment(sketch, "E185.MirrorCS", {"start": v(4617, 6029.3) * mm, "end": v(2638.84, 6029.3) * mm});
            skLineSegment(sketch, "E186.MirrorCS", {"start": v(-2622, 16163.9) * mm, "end": v(-1809.2, 16163.9) * mm});
            skArc(sketch, "E187.MirrorCS", {"start": v(578.4, 575.85) * mm, "mid": v(1153.13, 813.91) * mm, "end": v(1391.2, 1388.65) * mm});
            skLineSegment(sketch, "E188.MirrorCS", {"start": v(2562.64, 4581.5) * mm, "end": v(-2622, 4581.5) * mm});
            skLineSegment(sketch, "E189.MirrorCS", {"start": v(4540.8, 15249.5) * mm, "end": v(1035.6, 15249.5) * mm});
            skLineSegment(sketch, "E190.MirrorCS", {"start": v(4540.8, 1388.65) * mm, "end": v(1645.2, 1388.65) * mm});
            skLineSegment(sketch, "E191.MirrorCS", {"start": v(-4450.8, 1388.65) * mm, "end": v(-4450.8, -2116.55) * mm});
            skLineSegment(sketch, "E192.MirrorCS", {"start": v(-2622, 12049.1) * mm, "end": v(-2622, 6105.5) * mm});
            skLineSegment(sketch, "E193.MirrorCS", {"start": v(2715.04, 5953.1) * mm, "end": v(2715.04, 4581.5) * mm});
            skLineSegment(sketch, "E194.MirrorCS", {"start": v(-2622, 13115.9) * mm, "end": v(-1809.2, 13115.9) * mm});
            skLineSegment(sketch, "E195.MirrorCS", {"start": v(4540.8, 12049.1) * mm, "end": v(1035.6, 12049.1) * mm});
            skLineSegment(sketch, "E196.MirrorCS", {"start": v(4540.8, 13115.9) * mm, "end": v(3728, 13115.9) * mm});
            skLineSegment(sketch, "E197.MirrorCS", {"start": v(-2698.2, 15173.3) * mm, "end": v(959.4, 15173.3) * mm});
            skLineSegment(sketch, "E198.MirrorCS", {"start": v(4540.8, -2116.55) * mm, "end": v(4540.8, 1388.65) * mm});
            skLineSegment(sketch, "E199", {"start": v(7665, 12125.3) * mm, "end": v(14980.2, 12125.3) * mm});
            skLineSegment(sketch, "E200", {"start": v(7665, 9255.1) * mm, "end": v(7741.2, 9255.1) * mm});
            skLineSegment(sketch, "E201", {"start": v(7665, 9255.1) * mm, "end": v(7665, 9077.3) * mm});
            skLineSegment(sketch, "E202", {"start": v(7665, 12125.3) * mm, "end": v(11322.6, 12125.3) * mm});
            skLineSegment(sketch, "E203", {"start": v(7665, 12125.3) * mm, "end": v(7665, 9255.1) * mm});
            skLineSegment(sketch, "E204", {"start": v(7741.2, 12049.1) * mm, "end": v(7741.2, 9153.5) * mm});
            skLineSegment(sketch, "E205", {"start": v(-2698.2, 12125.3) * mm, "end": v(4617, 12125.3) * mm});
            skLineSegment(sketch, "E206", {"start": v(4617, 12125.3) * mm, "end": v(4617, 9077.3) * mm});
            skLineSegment(sketch, "E207", {"start": v(4540.8, 12049.1) * mm, "end": v(4540.8, 9153.5) * mm});
            skLineSegment(sketch, "E208", {"start": v(1492.85, 20126.15) * mm, "end": v(1645.25, 20126.15) * mm});
            skLineSegment(sketch, "E209", {"start": v(1645.25, 23631.35) * mm, "end": v(1492.85, 23631.35) * mm});
            skLineSegment(sketch, "E210", {"start": v(-1555.15, 23631.35) * mm, "end": v(-1402.75, 23631.35) * mm});
            skLineSegment(sketch, "E211", {"start": v(-1402.75, 20126.15) * mm, "end": v(-1555.15, 20126.15) * mm});
            skSolve(sketch);
        }
        {
            var Q0;
            Q0=makeQuery(id+"F0.imprint","IMPRINT",FACE,{"disambiguationData":[TD([[makeQuery(id+"F0.imprint","IMPRINT",EDGE,{"derivedFrom":sQuery(id+"F0.wireOp",EDGE,"E0.bottom")}),1.0]])]});
            var Q1;
            {var subQ1=sQuery(id+"F0.wireOp",EDGE,"E0.right");Q1=makeQuery(id+"F0.imprint","IMPRINT",FACE,{"disambiguationData":[TD([[makeQuery(id+"F0.imprint","IMPRINT",EDGE,{"derivedFrom":subQ1}),-1.0]])]});}
            var Q2;
            {var subQ1=sQuery(id+"F0.wireOp",EDGE,"E47.1.0.9");Q2=makeQuery(id+"F0.imprint","IMPRINT",FACE,{"disambiguationData":[TD([[makeQuery(id+"F0.imprint","IMPRINT",EDGE,{"derivedFrom":subQ1}),1.0]])]});}
            var Q3;
            {var subQ3=sQuery(id+"F0.wireOp",EDGE,"E4.right");Q3=makeQuery(id+"F0.imprint","IMPRINT",FACE,{"disambiguationData":[TD([[makeQuery(id+"F0.imprint","IMPRINT",EDGE,{"derivedFrom":subQ3}),1.0]])]});}
            var Q4;
            {var subQ5=sQuery(id+"F0.wireOp",EDGE,"E182.MirrorCS");Q4=makeQuery(id+"F0.imprint","IMPRINT",FACE,{"disambiguationData":[TD([[makeQuery(id+"F0.imprint","IMPRINT",EDGE,{"derivedFrom":subQ5}),1.0]])]});}
            var Q5;
            {var subQ6=sQuery(id+"F0.wireOp",EDGE,"E4.top");Q5=makeQuery(id+"F0.imprint","IMPRINT",FACE,{"disambiguationData":[TD([[makeQuery(id+"F0.imprint","IMPRINT",EDGE,{"derivedFrom":subQ6}),1.0]])]});}
            var Q6;
            {var subQ10=sQuery(id+"F0.wireOp",EDGE,"E2.top");Q6=makeQuery(id+"F0.imprint","IMPRINT",FACE,{"disambiguationData":[TD([[makeQuery(id+"F0.imprint","IMPRINT",EDGE,{"derivedFrom":subQ10}),-1.0]])]});}
            var Q7;
            Q7=makeQuery(id+"F0.imprint","IMPRINT",FACE,{"disambiguationData":[TD([[makeQuery(id+"F0.imprint","IMPRINT",EDGE,{"derivedFrom":sQuery(id+"F0.wireOp",EDGE,"E2.top")}),1.0]])]});
            var Q8;
            {var subQ2=sQuery(id+"F0.wireOp",EDGE,"E16.0.2.2");Q8=makeQuery(id+"F0.imprint","IMPRINT",FACE,{"disambiguationData":[TD([[makeQuery(id+"F0.imprint","IMPRINT",EDGE,{"derivedFrom":subQ2}),-1.0]])]});}
            var Q9;
            {var subQ1=sQuery(id+"F0.wireOp",EDGE,"E16.0.2.4");Q9=makeQuery(id+"F0.imprint","IMPRINT",FACE,{"disambiguationData":[TD([[makeQuery(id+"F0.imprint","IMPRINT",EDGE,{"derivedFrom":subQ1}),1.0]])]});}
            var Q10;
            Q10=makeQuery(id+"F0.imprint","IMPRINT",FACE,{"disambiguationData":[TD([[makeQuery(id+"F0.imprint","IMPRINT",EDGE,{"derivedFrom":sQuery(id+"F0.wireOp",EDGE,"E16.0.3.2")}),-1.0]])]});
            var Q11;
            {var subQ1=sQuery(id+"F0.wireOp",EDGE,"E16.0.3.1");Q11=makeQuery(id+"F0.imprint","IMPRINT",FACE,{"disambiguationData":[TD([[makeQuery(id+"F0.imprint","IMPRINT",EDGE,{"derivedFrom":subQ1}),1.0]])]});}
            var Q12;
            {var subQ1=sQuery(id+"F0.wireOp",EDGE,"E49.1.0.8");Q12=makeQuery(id+"F0.imprint","IMPRINT",FACE,{"disambiguationData":[TD([[makeQuery(id+"F0.imprint","IMPRINT",EDGE,{"derivedFrom":subQ1}),1.0]])]});}
            var Q13;
            {var subQ1=sQuery(id+"F0.wireOp",EDGE,"E49.2.0.8");Q13=makeQuery(id+"F0.imprint","IMPRINT",FACE,{"disambiguationData":[TD([[makeQuery(id+"F0.imprint","IMPRINT",EDGE,{"derivedFrom":subQ1}),1.0]])]});}
            var Q14;
            {var subQ5=sQuery(id+"F0.wireOp",EDGE,"E48.1.0.12");Q14=makeQuery(id+"F0.imprint","IMPRINT",FACE,{"disambiguationData":[TD([[makeQuery(id+"F0.imprint","IMPRINT",EDGE,{"derivedFrom":subQ5}),-1.0]])]});}
            var Q15;
            {var subQ1=sQuery(id+"F0.wireOp",EDGE,"E48.1.0.12");Q15=makeQuery(id+"F0.imprint","IMPRINT",FACE,{"disambiguationData":[TD([[makeQuery(id+"F0.imprint","IMPRINT",EDGE,{"derivedFrom":subQ1}),1.0]])]});}
            var Q16;
            {var subQ5=sQuery(id+"F0.wireOp",EDGE,"E48.2.0.9");Q16=makeQuery(id+"F0.imprint","IMPRINT",FACE,{"disambiguationData":[TD([[makeQuery(id+"F0.imprint","IMPRINT",EDGE,{"derivedFrom":subQ5}),1.0]])]});}
            var Q17;
            {var subQ7=sQuery(id+"F0.wireOp",EDGE,"E50.2.0.3");Q17=makeQuery(id+"F0.imprint","IMPRINT",FACE,{"disambiguationData":[TD([[makeQuery(id+"F0.imprint","IMPRINT",EDGE,{"derivedFrom":subQ7}),1.0]])]});}
            var Q18;
            {var subQ5=sQuery(id+"F0.wireOp",EDGE,"E48.2.0.9");Q18=makeQuery(id+"F0.imprint","IMPRINT",FACE,{"disambiguationData":[TD([[makeQuery(id+"F0.imprint","IMPRINT",EDGE,{"derivedFrom":subQ5}),1.0]])]});}
            var Q19;
            {var subQ3=sQuery(id+"F0.wireOp",EDGE,"E16.0.2.1");Q19=makeQuery(id+"F0.imprint","IMPRINT",FACE,{"disambiguationData":[TD([[makeQuery(id+"F0.imprint","IMPRINT",EDGE,{"derivedFrom":subQ3}),1.0]])]});}
            var Q20;
            {var subQ13=sQuery(id+"F0.wireOp",EDGE,"E2.right");Q20=makeQuery(id+"F0.imprint","IMPRINT",FACE,{"disambiguationData":[TD([[makeQuery(id+"F0.imprint","IMPRINT",EDGE,{"derivedFrom":subQ13}),-1.0]])]});}
            var Q21;
            {var subQ4=sQuery(id+"F0.wireOp",EDGE,"E68.MirrorCS");Q21=makeQuery(id+"F0.imprint","IMPRINT",FACE,{"disambiguationData":[TD([[makeQuery(id+"F0.imprint","IMPRINT",EDGE,{"derivedFrom":subQ4}),-1.0]])]});}
            var Q22;
            {var subQ1=sQuery(id+"F0.wireOp",EDGE,"E69.MirrorCS");Q22=makeQuery(id+"F0.imprint","IMPRINT",FACE,{"disambiguationData":[TD([[makeQuery(id+"F0.imprint","IMPRINT",EDGE,{"derivedFrom":subQ1}),-1.0]])]});}
            var Q23;
            {var subQ5=sQuery(id+"F0.wireOp",EDGE,"E71.MirrorCS");Q23=makeQuery(id+"F0.imprint","IMPRINT",FACE,{"disambiguationData":[TD([[makeQuery(id+"F0.imprint","IMPRINT",EDGE,{"derivedFrom":subQ5}),-1.0]])]});}
            var Q24;
            {var subQ3=sQuery(id+"F0.wireOp",EDGE,"E95.MirrorCS");Q24=makeQuery(id+"F0.imprint","IMPRINT",FACE,{"disambiguationData":[TD([[makeQuery(id+"F0.imprint","IMPRINT",EDGE,{"derivedFrom":subQ3}),1.0]])]});}
            var Q25;
            {var subQ6=sQuery(id+"F0.wireOp",EDGE,"E64.MirrorCS");Q25=makeQuery(id+"F0.imprint","IMPRINT",FACE,{"disambiguationData":[TD([[makeQuery(id+"F0.imprint","IMPRINT",EDGE,{"derivedFrom":subQ6}),1.0]])]});}
            var Q26;
            {var subQ8=sQuery(id+"F0.wireOp",EDGE,"E61.MirrorCS");Q26=makeQuery(id+"F0.imprint","IMPRINT",FACE,{"disambiguationData":[TD([[makeQuery(id+"F0.imprint","IMPRINT",EDGE,{"derivedFrom":subQ8}),-1.0]])]});}
            var Q27;
            {var subQ12=sQuery(id+"F0.wireOp",EDGE,"E59.MirrorCS");Q27=makeQuery(id+"F0.imprint","IMPRINT",FACE,{"disambiguationData":[TD([[makeQuery(id+"F0.imprint","IMPRINT",EDGE,{"derivedFrom":subQ12}),1.0]])]});}
            var Q28;
            {var subQ1=sQuery(id+"F0.wireOp",EDGE,"E76.MirrorCS");Q28=makeQuery(id+"F0.imprint","IMPRINT",FACE,{"disambiguationData":[TD([[makeQuery(id+"F0.imprint","IMPRINT",EDGE,{"derivedFrom":subQ1}),-1.0]])]});}
            var Q29;
            Q29=makeQuery(id+"F0.imprint","IMPRINT",FACE,{"disambiguationData":[TD([[makeQuery(id+"F0.imprint","IMPRINT",EDGE,{"derivedFrom":sQuery(id+"F0.wireOp",EDGE,"E80.MirrorCS")}),-1.0]])]});
            var Q30;
            {var subQ1=sQuery(id+"F0.wireOp",EDGE,"E65.MirrorCS");Q30=makeQuery(id+"F0.imprint","IMPRINT",FACE,{"disambiguationData":[TD([[makeQuery(id+"F0.imprint","IMPRINT",EDGE,{"derivedFrom":subQ1}),-1.0]])]});}
            var Q31;
            {var subQ4=sQuery(id+"F0.wireOp",EDGE,"E63.MirrorCS");Q31=makeQuery(id+"F0.imprint","IMPRINT",FACE,{"disambiguationData":[TD([[makeQuery(id+"F0.imprint","IMPRINT",EDGE,{"derivedFrom":subQ4}),1.0]])]});}
            var Q32;
            {var subQ9=sQuery(id+"F0.wireOp",EDGE,"E62.MirrorCS");Q32=makeQuery(id+"F0.imprint","IMPRINT",FACE,{"disambiguationData":[TD([[makeQuery(id+"F0.imprint","IMPRINT",EDGE,{"derivedFrom":subQ9}),-1.0]])]});}
            var Q33;
            {var subQ3=sQuery(id+"F0.wireOp",EDGE,"E50.2.0.15");Q33=makeQuery(id+"F0.imprint","IMPRINT",FACE,{"disambiguationData":[TD([[makeQuery(id+"F0.imprint","IMPRINT",EDGE,{"derivedFrom":subQ3}),-1.0]])]});}
            var Q34;
            {var subQ0=sQuery(id+"F0.wireOp",EDGE,"E50.1.0.15");Q34=makeQuery(id+"F0.imprint","IMPRINT",FACE,{"disambiguationData":[TD([[makeQuery(id+"F0.imprint","IMPRINT",EDGE,{"derivedFrom":subQ0}),-1.0]])]});}
            extrude(context, id + "F1", {"entities" : qUnion([Q0, Q1, Q2, Q3, Q4, Q5, Q6, Q7, Q8, Q9, Q10, Q11, Q12, Q13, Q14, Q15, Q16, Q17, Q18, Q19, Q20, Q21, Q22, Q23, Q24, Q25, Q26, Q27, Q28, Q29, Q30, Q31, Q32, Q33, Q34]), "depth" : 2438.4 * mm, "offsetDistance" : 30.48 * mm});
        }
    });
